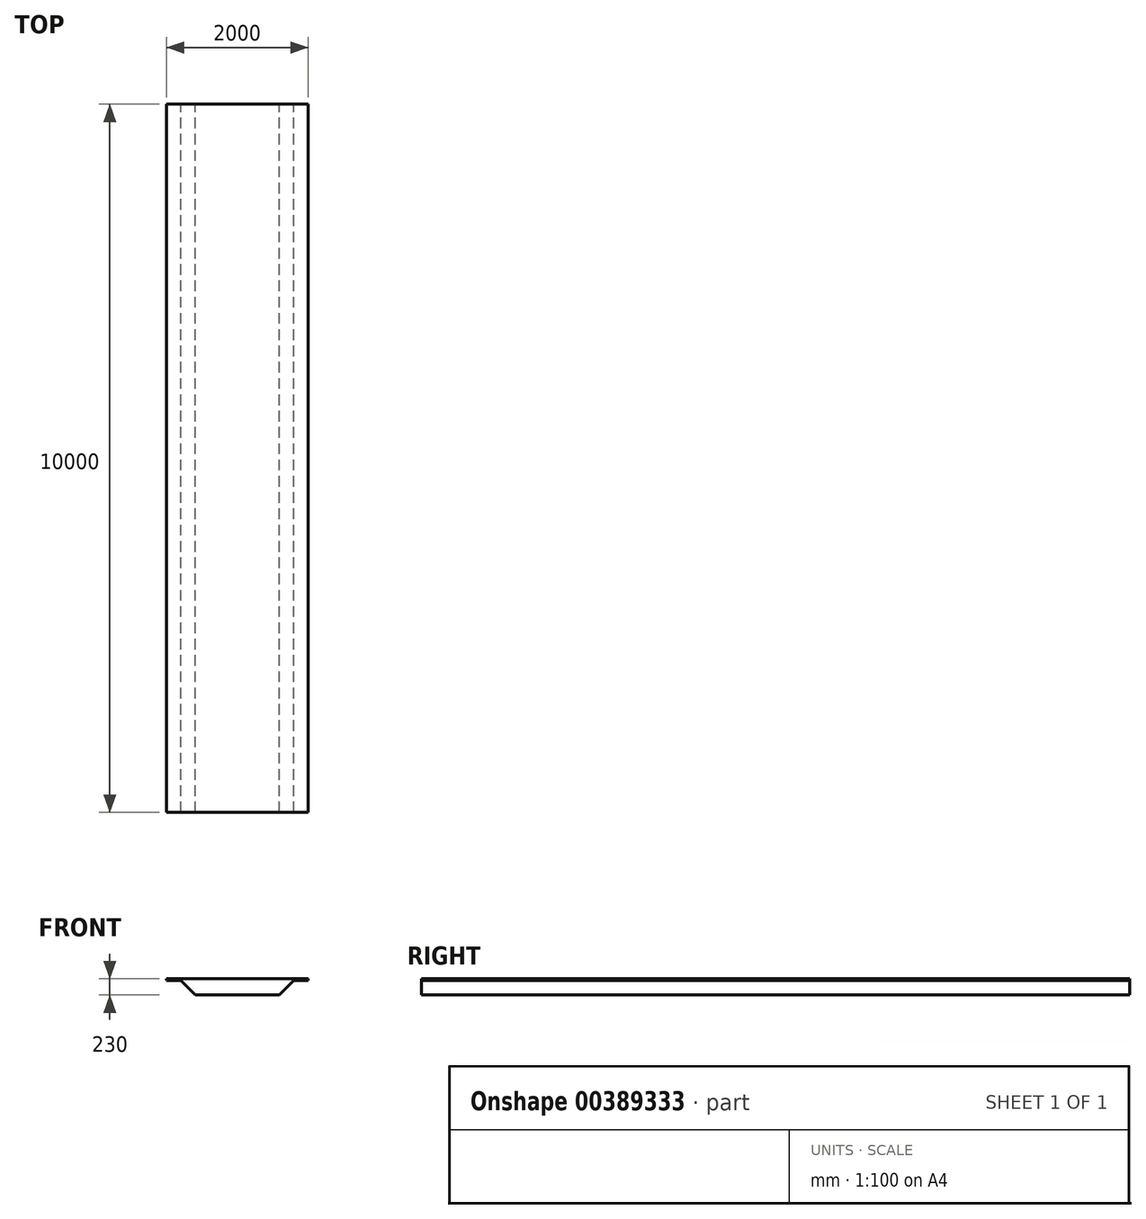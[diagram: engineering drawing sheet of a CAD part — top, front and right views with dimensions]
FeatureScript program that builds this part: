
annotation { "Feature Type Name" : "Feature", "Feature Type Description" : "" }
export const myFeature = defineFeature(function(context is Context, id is Id, definition is map)
    precondition{}
    {
        {
            var Q0;
            Q0=qCreatedBy(makeId("Front.planeOp"),FACE);
            var sketch = newSketch(context, id + "F0", { "sketchPlane" : qUnion([Q0])});
            skLineSegment(sketch, "E0", {"start": v(-989.26, 131.54) * mm, "end": v(1010.74, 131.54) * mm});
            skLineSegment(sketch, "E1", {"start": v(-989.26, 131.54) * mm, "end": v(-989.26, -98.46) * mm});
            skLineSegment(sketch, "E2", {"start": v(-989.26, -98.46) * mm, "end": v(1010.74, -98.46) * mm});
            skLineSegment(sketch, "E3", {"start": v(1010.74, -98.46) * mm, "end": v(1010.74, 131.54) * mm});
            skLineSegment(sketch, "E4.bottom", {"start": v(-989.26, -98.46) * mm, "end": v(-789.26, -98.46) * mm, "construction": true});
            skLineSegment(sketch, "E4.top", {"start": v(-989.26, 106.54) * mm, "end": v(-789.26, 106.54) * mm});
            skLineSegment(sketch, "E4.left", {"start": v(-989.26, -98.46) * mm, "end": v(-989.26, 106.54) * mm, "construction": true});
            skLineSegment(sketch, "E4.right", {"start": v(-789.26, -98.46) * mm, "end": v(-789.26, 106.54) * mm});
            skLineSegment(sketch, "E5.bottom", {"start": v(1010.74, -98.46) * mm, "end": v(810.74, -98.46) * mm});
            skLineSegment(sketch, "E5.top", {"start": v(1010.74, 106.54) * mm, "end": v(810.74, 106.54) * mm});
            skLineSegment(sketch, "E5.left", {"start": v(1010.74, -98.46) * mm, "end": v(1010.74, 106.54) * mm});
            skLineSegment(sketch, "E5.right", {"start": v(810.74, -98.46) * mm, "end": v(810.74, 106.54) * mm});
            skLineSegment(sketch, "E6", {"start": v(-789.26, -98.46) * mm, "end": v(-584.26, -98.46) * mm});
            skLineSegment(sketch, "E7", {"start": v(-584.26, -98.46) * mm, "end": v(810.74, -98.46) * mm});
            skLineSegment(sketch, "E8", {"start": v(605.74, -98.46) * mm, "end": v(810.74, -98.46) * mm});
            skLineSegment(sketch, "E9", {"start": v(-789.26, 106.54) * mm, "end": v(-584.26, -98.46) * mm});
            skLineSegment(sketch, "E10", {"start": v(810.74, 106.54) * mm, "end": v(605.74, -98.46) * mm});
            skLineSegment(sketch, "E11", {"start": v(-584.26, -98.46) * mm, "end": v(605.74, -98.46) * mm});
            skSolve(sketch);
        }
        {
            var Q0;
            {var subQ1=sQuery(id+"F0.wireOp",EDGE,"E0");Q0=makeQuery(id+"F0.imprint","IMPRINT",FACE,{"disambiguationData":[TD([[makeQuery(id+"F0.imprint","IMPRINT",EDGE,{"derivedFrom":subQ1}),-1.0]])]});}
            extrude(context, id + "F1", {"entities" : qUnion([Q0]), "depth" : 10000 * mm});
        }
    });
